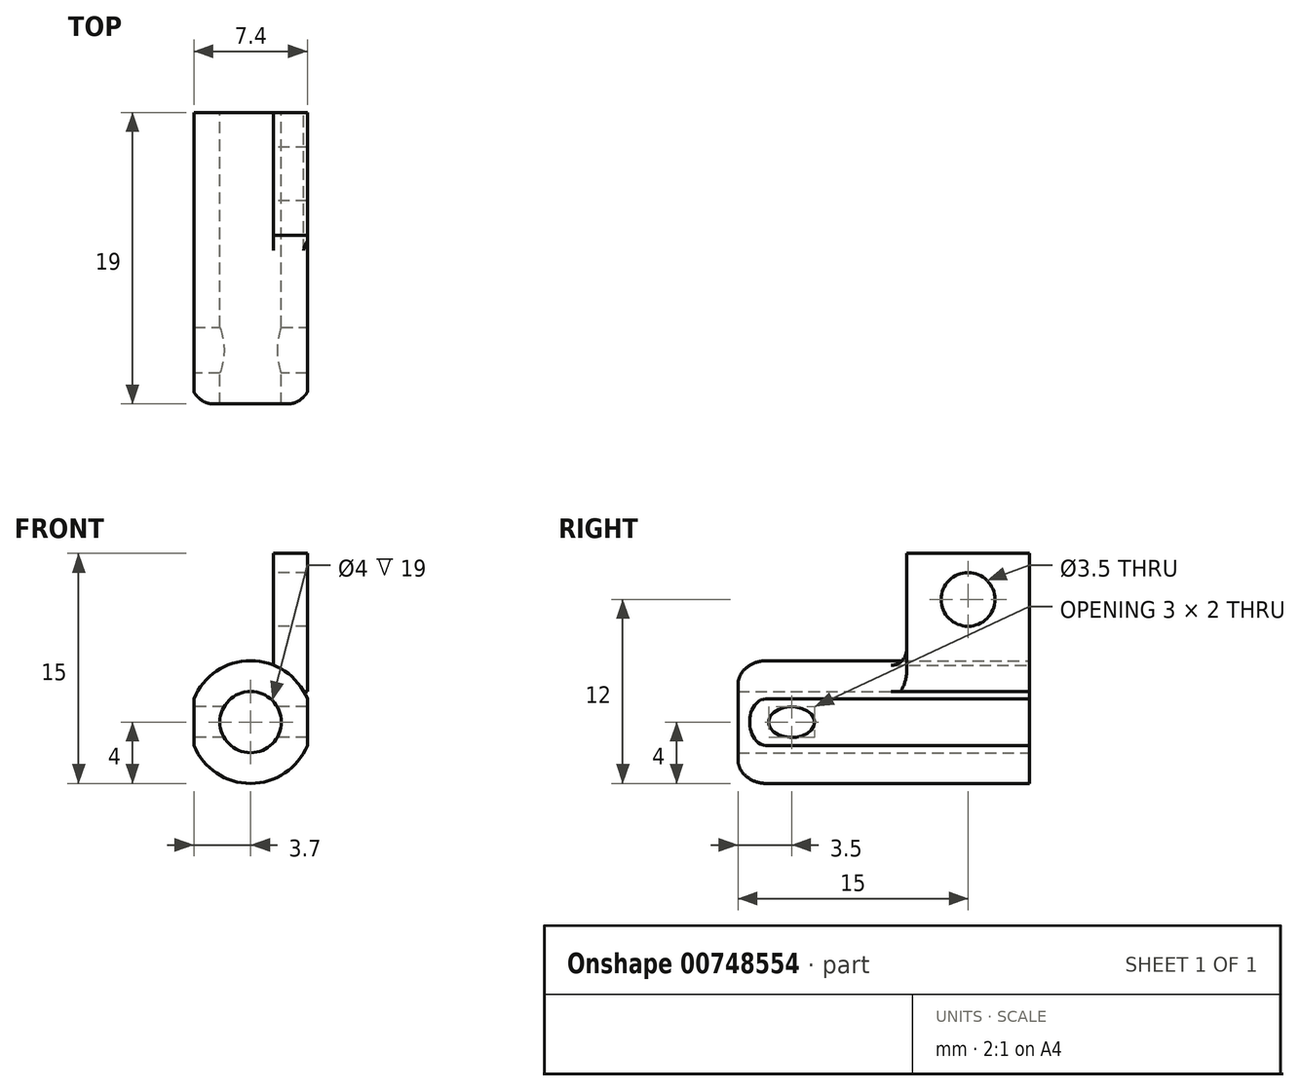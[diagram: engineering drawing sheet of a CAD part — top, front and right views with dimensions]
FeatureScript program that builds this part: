
annotation { "Feature Type Name" : "Feature", "Feature Type Description" : "" }
export const myFeature = defineFeature(function(context is Context, id is Id, definition is map)
    precondition{}
    {
        {
            var Q0;
            Q0=qCreatedBy(makeId("Right.planeOp"),FACE);
            var sketch = newSketch(context, id + "F0", { "sketchPlane" : qUnion([Q0])});
            skLineSegment(sketch, "E0.bottom", {"start": v(-4, 3) * mm, "end": v(4, 3) * mm});
            skLineSegment(sketch, "E0.top", {"start": v(-4, -6) * mm, "end": v(4, -6) * mm});
            skLineSegment(sketch, "E0.left", {"start": v(-4, 3) * mm, "end": v(-4, -6) * mm});
            skLineSegment(sketch, "E0.right", {"start": v(4, 3) * mm, "end": v(4, -6) * mm});
            skCircle(sketch, "E1", {"center": v(0, 0) * mm, "radius": 1.75 * mm});
            skSolve(sketch);
        }
        {
            var Q0;
            Q0=makeQuery(id+"F0.imprint","IMPRINT",FACE,{"disambiguationData":[TD([[makeQuery(id+"F0.imprint","IMPRINT",EDGE,{"derivedFrom":sQuery(id+"F0.wireOp",EDGE,"E0.bottom")}),-1.0]])]});
            extrude(context, id + "F1", {"entities" : qUnion([Q0]), "depth" : 2.2 * mm, "offsetDistance" : 25 * mm});
        }
        {
            var Q0;
            Q0=qCreatedBy(makeId("Front.planeOp"),FACE);
            var sketch = newSketch(context, id + "F2", { "sketchPlane" : qUnion([Q0])});
            skCircle(sketch, "E2", {"center": v(-1.5, -8) * mm, "radius": 2 * mm});
            skCircle(sketch, "E3", {"center": v(-1.5, -8) * mm, "radius": 4 * mm});
            skLineSegment(sketch, "E4.0.0", {"start": v(0, 3) * mm, "end": v(0, -6) * mm});
            skLineSegment(sketch, "E4.0.1", {"start": v(0, -6) * mm, "end": v(2.2, -6) * mm});
            skLineSegment(sketch, "E4.0.2", {"start": v(2.2, -6) * mm, "end": v(2.2, 3) * mm});
            skLineSegment(sketch, "E4.0.3", {"start": v(2.2, 3) * mm, "end": v(0, 3) * mm});
            skLineSegment(sketch, "E5", {"start": v(2.2, -6) * mm, "end": v(2.2, -9.52) * mm});
            skSolve(sketch);
        }
        {
            var Q0;
            Q0=makeQuery(id+"F2.imprint","IMPRINT",FACE,{"disambiguationData":[TD([[makeQuery(id+"F2.imprint","IMPRINT",EDGE,{"derivedFrom":sQuery(id+"F2.wireOp",EDGE,"E2")}),-1.0]])]});
            var Q1;
            {var subQ0=sQuery(id+"F2.wireOp",EDGE,"E5");var subQ1=sQuery(id+"F2.wireOp",EDGE,"E3");var subQ2=makeQuery(id+"F2.imprint","INTERSECT",VERTEX,{"disambiguationData":[OD(1.0)],"derivedFrom":[subQ1,subQ0]});Q1=makeQuery(id+"F2.imprint","IMPRINT",FACE,{"disambiguationData":[TD([[makeQuery(id+"F2.imprint","IMPRINT",EDGE,{"disambiguationData":[TD([[subQ2,-1.0]])],"derivedFrom":subQ1}),-1.0]])]});}
            var Q2;
            Q2=makeQuery(id+"F1.opExtrude","SWEPT_FACE",FACE,{"disambiguationData":[OSD([sQuery(id+"F0.wireOp",EDGE,"E0.left")])]});
            var Q3;
            Q3=makeQuery(id+"F1.opExtrude","SWEPT_FACE",FACE,{"disambiguationData":[OSD([sQuery(id+"F0.wireOp",EDGE,"E0.right")])]});
            extrude(context, id + "F3", {"entities" : qUnion([Q0, Q1]), "operationType" : NewBodyOperationType.ADD, "endBound" : BoundingType.UP_TO_SURFACE, "depth" : 25 * mm, "endBoundEntityFace" : qUnion([Q2]), "offsetDistance" : 25 * mm, "hasSecondDirection" : true, "secondDirectionBound" : SecondDirectionBoundingType.UP_TO_SURFACE, "secondDirectionOppositeDirection" : true, "secondDirectionDepth" : 25 * mm, "secondDirectionBoundEntityFace" : qUnion([Q3])});
        }
        {
            var Q0;
            Q0=makeQuery(id+"F2.imprint","IMPRINT",FACE,{"disambiguationData":[TD([[makeQuery(id+"F2.imprint","IMPRINT",EDGE,{"derivedFrom":sQuery(id+"F2.wireOp",EDGE,"E2")}),-1.0]])]});
            var Q1;
            {var subQ0=sQuery(id+"F2.wireOp",EDGE,"E4.0.0");var subQ1=sQuery(id+"F2.wireOp",EDGE,"E3");var subQ2=makeQuery(id+"F2.imprint","INTERSECT",VERTEX,{"derivedFrom":[subQ1,subQ0]});Q1=makeQuery(id+"F2.imprint","IMPRINT",FACE,{"disambiguationData":[TD([[makeQuery(id+"F2.imprint","IMPRINT",EDGE,{"disambiguationData":[TD([[subQ2,1.0]])],"derivedFrom":subQ1}),1.0]])]});}
            extrude(context, id + "F4", {"entities" : qUnion([Q0, Q1]), "operationType" : NewBodyOperationType.ADD, "depth" : 15 * mm, "offsetDistance" : 25 * mm});
        }
        {
            var Q0;
            Q0=makeQuery(id+"F4.opExtrude","CAP_EDGE",EDGE,{"disambiguationData":[OSD([sQuery(id+"F2.wireOp",EDGE,"E3")])],"isStart":false});
            chamfer(context, id + "F5", {"entities" : qUnion([Q0]), "chamferType" : ChamferType.TWO_OFFSETS, "width1" : 1 * mm, "oppositeDirection" : false, "width2" : 1 * mm, "tangentPropagation" : true});
        }
        {
            var Q0;
            {var subQ0=sQuery(id+"F2.wireOp",EDGE,"E3");Q0=makeQuery(id+"F5.opChamfer","BLEND_EDGE",EDGE,{"blendedFrom":[makeQuery(id+"F4.opExtrude","CAP_EDGE",EDGE,{"disambiguationData":[OSD([subQ0])],"isStart":false}),makeQuery(id+"F4.opExtrude","CAP_FACE",FACE,{"disambiguationData":[OSD([sQuery(id+"F2.wireOp",EDGE,"E2"),subQ0,sQuery(id+"F2.wireOp",EDGE,"E5")])],"isStart":false})],"blendedInto":[makeQuery(id+"F4.opExtrude","CAP_FACE",FACE,{"disambiguationData":[OSD([sQuery(id+"F2.wireOp",EDGE,"E2"),subQ0,sQuery(id+"F2.wireOp",EDGE,"E5")])],"isStart":false})]});}
            fillet(context, id + "F6", {"entities" : qUnion([Q0]), "radius" : 1.4 * mm, "tangentPropagation" : true, "allowEdgeOverflow" : false});
        }
        {
            var Q0;
            {var subQ0=sQuery(id+"F2.wireOp",EDGE,"E3");Q0=makeQuery(id+"F5.opChamfer","BLEND_EDGE",EDGE,{"blendedFrom":[makeQuery(id+"F4.opExtrude","CAP_EDGE",EDGE,{"disambiguationData":[OSD([subQ0])],"isStart":false}),makeQuery(id+"F4.boolean.opBoolean","MERGE",FACE,{"derivedFrom":[makeQuery(id+"F3.opExtrude","SWEPT_FACE",FACE,{"disambiguationData":[OSD([subQ0])]}),makeQuery(id+"F4.opExtrude","SWEPT_FACE",FACE,{"disambiguationData":[OSD([subQ0])]})]})],"blendedInto":[makeQuery(id+"F4.boolean.opBoolean","MERGE",FACE,{"derivedFrom":[makeQuery(id+"F3.opExtrude","SWEPT_FACE",FACE,{"disambiguationData":[OSD([subQ0])]}),makeQuery(id+"F4.opExtrude","SWEPT_FACE",FACE,{"disambiguationData":[OSD([subQ0])]})]})]});}
            fillet(context, id + "F7", {"entities" : qUnion([Q0]), "radius" : 2 * mm, "tangentPropagation" : true, "allowEdgeOverflow" : false});
        }
        {
            var Q0;
            {var subQ0=sQuery(id+"F2.wireOp",EDGE,"E3");Q0=makeQuery(id+"F4.boolean.opBoolean","INTERSECT",EDGE,{"derivedFrom":[makeQuery(id+"F3.boolean.opBoolean","MERGE",FACE,{"derivedFrom":[makeQuery(id+"F1.opExtrude","SWEPT_FACE",FACE,{"disambiguationData":[OSD([sQuery(id+"F0.wireOp",EDGE,"E0.left")])]}),makeQuery(id+"F3.opExtrude","CAP_FACE",FACE,{"disambiguationData":[OSD([sQuery(id+"F2.wireOp",EDGE,"E2"),subQ0,sQuery(id+"F2.wireOp",EDGE,"E4.0.0"),sQuery(id+"F2.wireOp",EDGE,"E4.0.1"),sQuery(id+"F2.wireOp",EDGE,"E5")])],"isStart":false})]}),makeQuery(id+"F4.opExtrude","SWEPT_FACE",FACE,{"disambiguationData":[OSD([subQ0])]})]});}
            var Q1;
            {var subQ0=sQuery(id+"F2.wireOp",EDGE,"E4.0.0");var subQ1=sQuery(id+"F2.wireOp",EDGE,"E3");Q1=makeQuery(id+"F3.opExtrude","TWEAK_EDGE",EDGE,{"derivedFrom":[makeQuery(id+"F2.imprint","IMPRINT",EDGE,{"disambiguationData":[TD([[makeQuery(id+"F2.imprint","INTERSECT",VERTEX,{"disambiguationData":[OD(0.0)],"derivedFrom":[subQ1,sQuery(id+"F2.wireOp",EDGE,"E5")]}),1.0]])],"derivedFrom":subQ1}),makeQuery(id+"F2.imprint","IMPRINT",EDGE,{"disambiguationData":[TD([[makeQuery(id+"F2.imprint","INTERSECT",VERTEX,{"derivedFrom":[subQ0,sQuery(id+"F2.wireOp",EDGE,"E4.0.1")]}),1.0]])],"derivedFrom":subQ0})]});}
            fillet(context, id + "F8", {"entities" : qUnion([Q0, Q1]), "radius" : 1 * mm, "tangentPropagation" : true, "allowEdgeOverflow" : false});
        }
        {
            var Q0;
            Q0=qCreatedBy(makeId("Right.planeOp"),FACE);
            var sketch = newSketch(context, id + "F9", { "sketchPlane" : qUnion([Q0])});
            skEllipse(sketch, "E6", {"center": v(-11.5, -8) * mm, "majorRadius": 1.5 * mm, "minorRadius": 1 * mm, "majorAxis": v(1, 0)});
            skSolve(sketch);
        }
        {
            var Q0;
            Q0 = qSketchRegion(id + "F9", true);
            extrude(context, id + "F10", {"entities" : qUnion([Q0]), "operationType" : NewBodyOperationType.REMOVE, "endBound" : BoundingType.THROUGH_ALL, "oppositeDirection" : true, "depth" : 25 * mm, "offsetDistance" : 25 * mm, "hasSecondDirection" : true, "secondDirectionBound" : SecondDirectionBoundingType.THROUGH_ALL, "secondDirectionOppositeDirection" : false, "secondDirectionDepth" : 25 * mm});
        }
        {
            var Q0;
            Q0=makeQuery(id+"F3.boolean.opBoolean","MERGE",FACE,{"derivedFrom":[makeQuery(id+"F1.opExtrude","SWEPT_FACE",FACE,{"disambiguationData":[OSD([sQuery(id+"F0.wireOp",EDGE,"E0.right")])]}),makeQuery(id+"F3.opExtrude","CAP_FACE",FACE,{"disambiguationData":[OSD([sQuery(id+"F2.wireOp",EDGE,"E2"),sQuery(id+"F2.wireOp",EDGE,"E3"),sQuery(id+"F2.wireOp",EDGE,"E4.0.0"),sQuery(id+"F2.wireOp",EDGE,"E4.0.1"),sQuery(id+"F2.wireOp",EDGE,"E5")])],"isStart":true})]});
            var sketch = newSketch(context, id + "F11", { "sketchPlane" : qUnion([Q0])});
            skCircle(sketch, "E7.0", {"center": v(1.5, -8) * mm, "radius": 4 * mm});
            skLineSegment(sketch, "E7.1", {"start": v(-2.2, -6) * mm, "end": v(-2.2, -9.52) * mm});
            skPoint(sketch, "E8", {"position": v(-2.2, -6.48) * mm});
            skLineSegment(sketch, "E9", {"start": v(-2.2, -6.48) * mm, "end": v(9.26, -6.48) * mm});
            skLineSegment(sketch, "E10", {"start": v(9.26, -6.48) * mm, "end": v(9.26, -9.52) * mm});
            skLineSegment(sketch, "E11", {"start": v(9.26, -9.52) * mm, "end": v(5.2, -9.52) * mm});
            skLineSegment(sketch, "E12", {"start": v(5.2, -9.52) * mm, "end": v(5.2, -6.48) * mm});
            skSolve(sketch);
        }
        {
            var Q0;
            {var subQ0=sQuery(id+"F11.wireOp",EDGE,"E12");Q0=makeQuery(id+"F11.imprint","IMPRINT",FACE,{"disambiguationData":[TD([[makeQuery(id+"F11.imprint","IMPRINT",EDGE,{"derivedFrom":subQ0}),-1.0]])]});}
            extrude(context, id + "F12", {"entities" : qUnion([Q0]), "operationType" : NewBodyOperationType.REMOVE, "oppositeDirection" : true, "depth" : 25 * mm, "offsetDistance" : 25 * mm});
        }
    });
